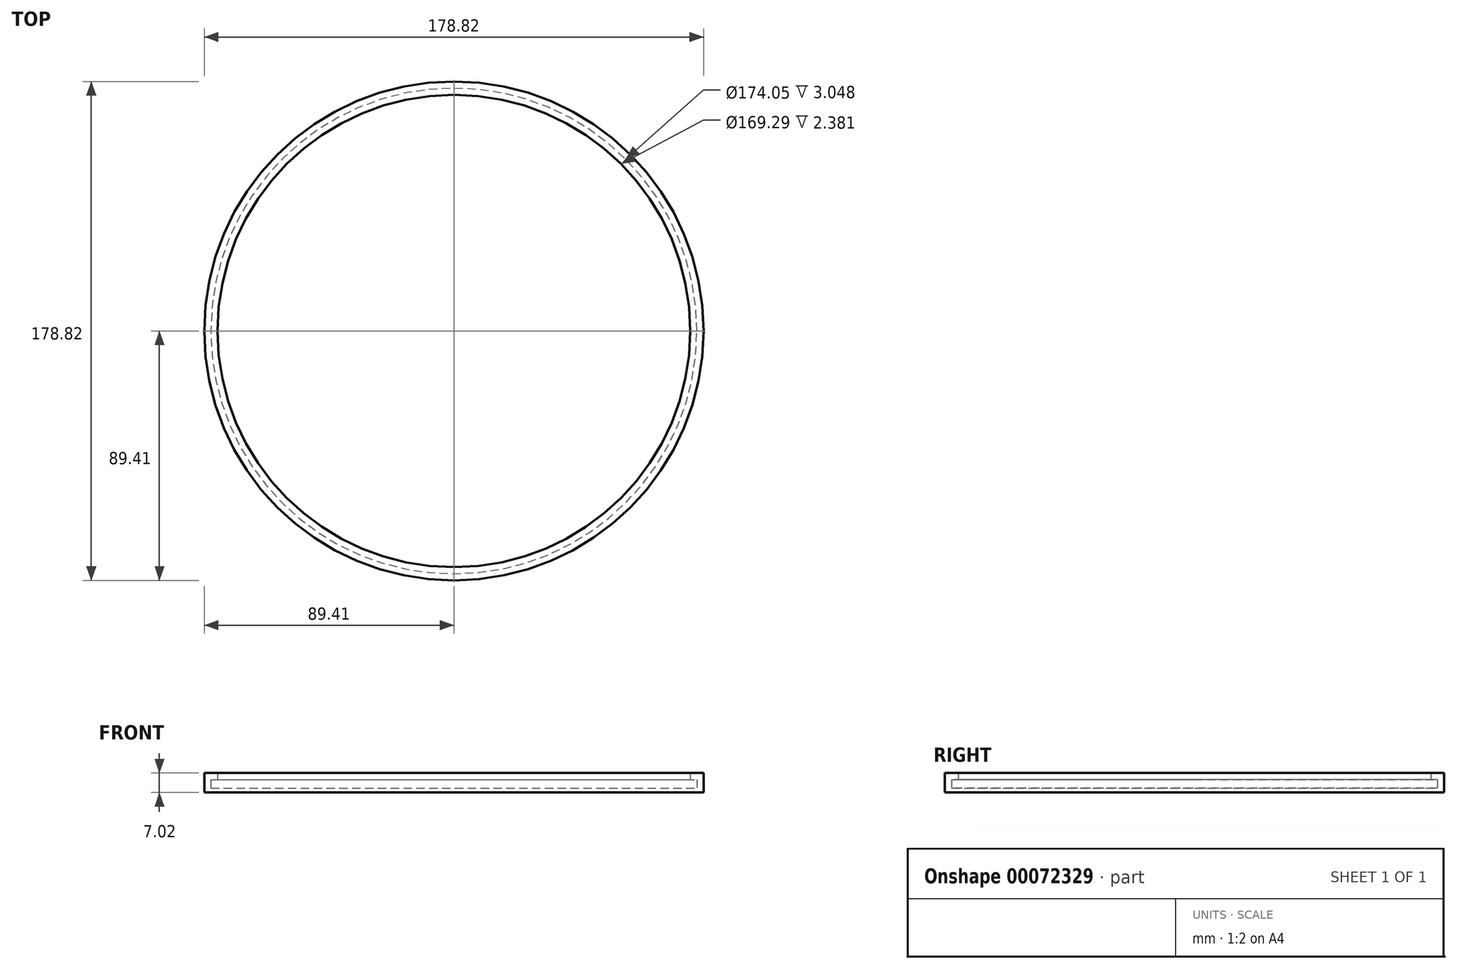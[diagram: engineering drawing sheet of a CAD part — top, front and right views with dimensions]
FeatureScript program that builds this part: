
annotation { "Feature Type Name" : "Feature", "Feature Type Description" : "" }
export const myFeature = defineFeature(function(context is Context, id is Id, definition is map)
    precondition{}
    {
        {
            var Q0;
            Q0=qCreatedBy(makeId("Front.planeOp"),FACE);
            var sketch = newSketch(context, id + "F0", { "sketchPlane" : qUnion([Q0])});
            skLineSegment(sketch, "E0", {"start": v(0, 0) * mm, "end": v(-89.4, 0) * mm});
            skLineSegment(sketch, "E1", {"start": v(-89.4, 0) * mm, "end": v(-89.4, 7.02) * mm});
            skLineSegment(sketch, "E2", {"start": v(-89.4, 7.02) * mm, "end": v(-84.65, 7.02) * mm});
            skLineSegment(sketch, "E3", {"start": v(-84.65, 7.02) * mm, "end": v(-84.65, 4.64) * mm});
            skLineSegment(sketch, "E4", {"start": v(-84.65, 4.64) * mm, "end": v(-87.03, 4.64) * mm});
            skLineSegment(sketch, "E5", {"start": v(-87.03, 4.64) * mm, "end": v(-87.03, 1.59) * mm});
            skLineSegment(sketch, "E6", {"start": v(-87.03, 1.59) * mm, "end": v(0, 1.59) * mm});
            skLineSegment(sketch, "E7", {"start": v(0, 0) * mm, "end": v(0, 1.59) * mm});
            skSolve(sketch);
        }
        {
            var Q0;
            Q0=makeQuery(id+"F0.imprint","IMPRINT",FACE,{"disambiguationData":[TD([[makeQuery(id+"F0.imprint","IMPRINT",EDGE,{"derivedFrom":sQuery(id+"F0.wireOp",EDGE,"E0")}),-1.0]])]});
            var Q1;
            Q1=sQuery(id+"F0.wireOp",EDGE,"E7");
            revolve(context, id + "F1", {"entities" : qUnion([Q0]), "axis" : qUnion([Q1]), "revolveType" : RevolveType.FULL});
        }
    });
